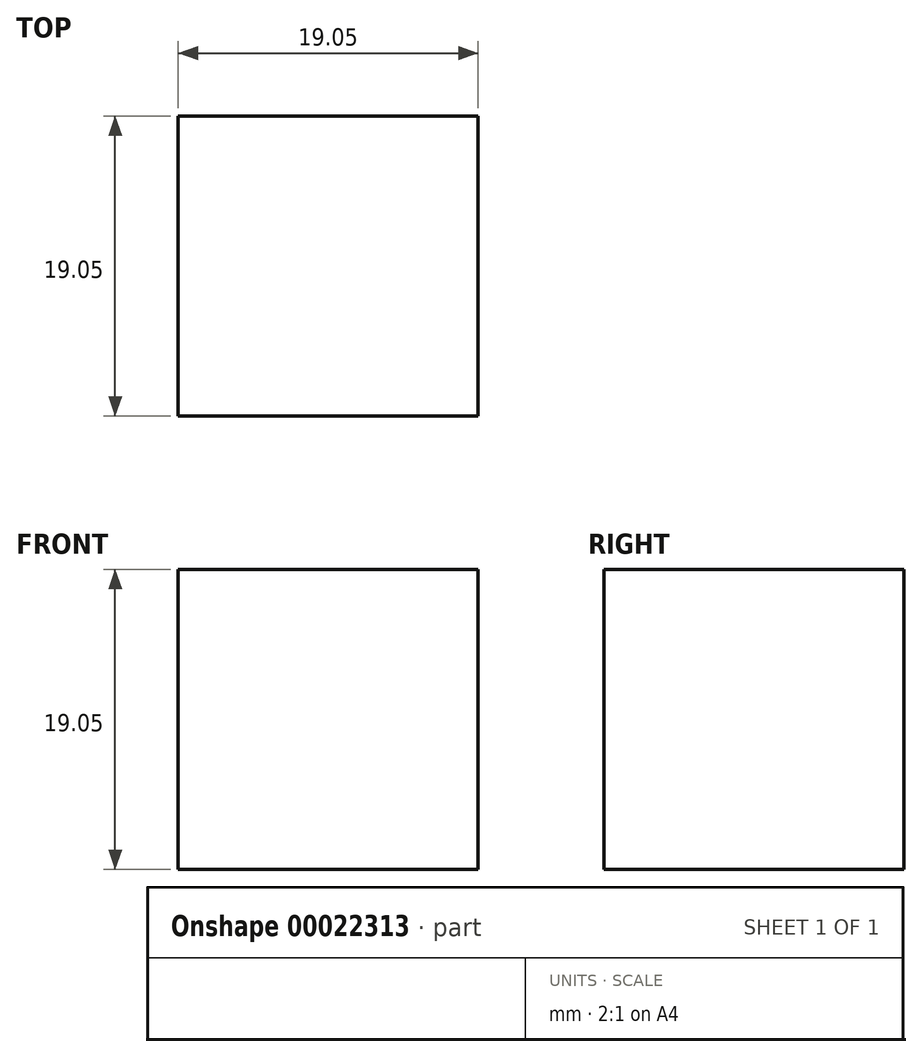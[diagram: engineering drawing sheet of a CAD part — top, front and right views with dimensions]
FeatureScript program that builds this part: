
annotation { "Feature Type Name" : "Feature", "Feature Type Description" : "" }
export const myFeature = defineFeature(function(context is Context, id is Id, definition is map)
    precondition{}
    {
        {
            var Q0;
            Q0=qCreatedBy(makeId("Top.planeOp"),FACE);
            var sketch = newSketch(context, id + "F0", { "sketchPlane" : qUnion([Q0])});
            skLineSegment(sketch, "E0.bottom", {"start": v(0, 0) * mm, "end": v(19.05, 0) * mm});
            skLineSegment(sketch, "E0.top", {"start": v(0, 19.05) * mm, "end": v(19.05, 19.05) * mm});
            skLineSegment(sketch, "E0.left", {"start": v(0, 0) * mm, "end": v(0, 19.05) * mm});
            skLineSegment(sketch, "E0.right", {"start": v(19.05, 0) * mm, "end": v(19.05, 19.05) * mm});
            skSolve(sketch);
        }
        {
            var Q0;
            Q0=makeQuery(id+"F0.imprint","IMPRINT",FACE,{"disambiguationData":[TD([[makeQuery(id+"F0.imprint","IMPRINT",EDGE,{"derivedFrom":sQuery(id+"F0.wireOp",EDGE,"E0.bottom")}),1.0]])]});
            extrude(context, id + "F1", {"entities" : qUnion([Q0]), "depth" : 19.05 * mm});
        }
    });
